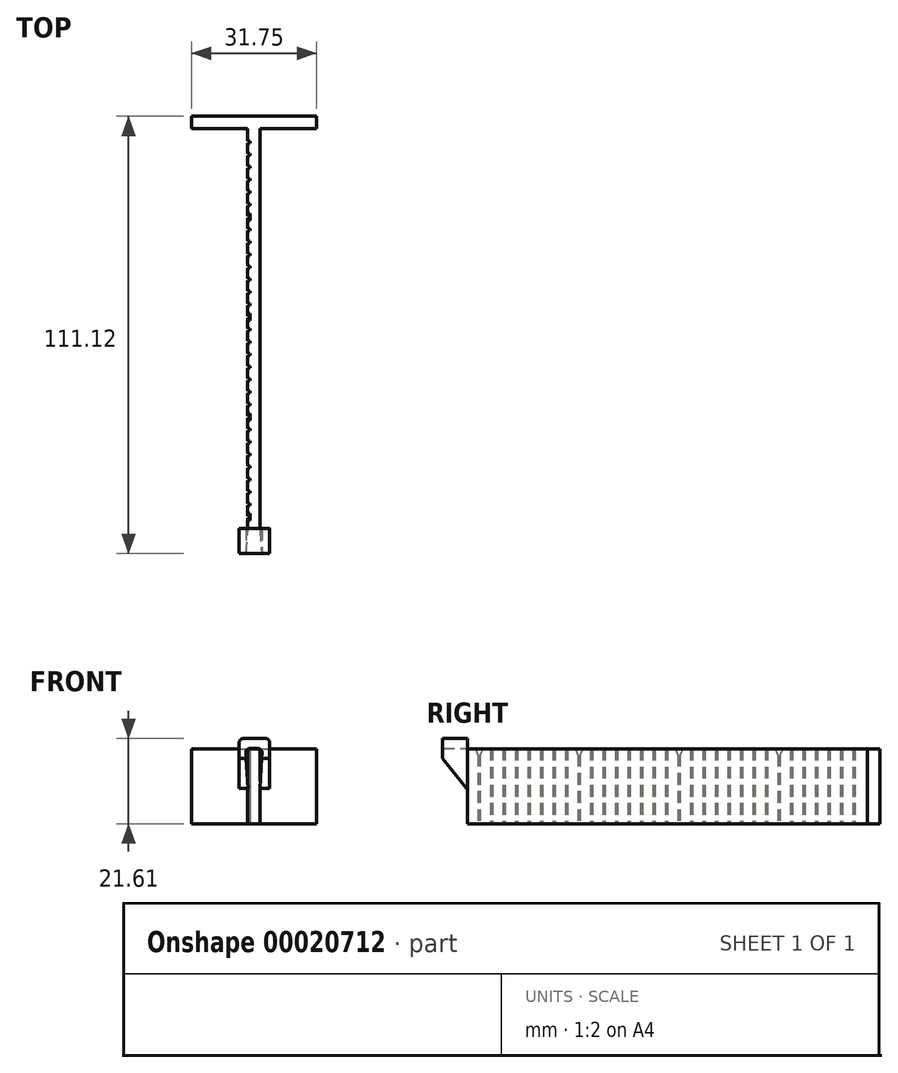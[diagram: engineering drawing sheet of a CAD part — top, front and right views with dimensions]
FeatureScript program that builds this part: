
annotation { "Feature Type Name" : "Feature", "Feature Type Description" : "" }
export const myFeature = defineFeature(function(context is Context, id is Id, definition is map)
    precondition{}
    {
        {
            var Q0;
            Q0=qCreatedBy(makeId("Top.planeOp"),FACE);
            var sketch = newSketch(context, id + "F0", { "sketchPlane" : qUnion([Q0])});
            skLineSegment(sketch, "E0.bottom", {"start": v(0, 0) * mm, "end": v(31.75, 0) * mm});
            skLineSegment(sketch, "E0.top", {"start": v(0, 3.18) * mm, "end": v(31.75, 3.18) * mm});
            skLineSegment(sketch, "E0.left", {"start": v(0, 0) * mm, "end": v(0, 3.18) * mm});
            skLineSegment(sketch, "E0.right", {"start": v(31.75, 0) * mm, "end": v(31.75, 3.18) * mm});
            skLineSegment(sketch, "E1.bottom", {"start": v(14.29, 0) * mm, "end": v(17.46, 0) * mm});
            skLineSegment(sketch, "E1.top", {"start": v(14.29, -101.6) * mm, "end": v(17.46, -101.6) * mm});
            skLineSegment(sketch, "E1.left", {"start": v(14.29, 0) * mm, "end": v(14.29, -101.6) * mm});
            skLineSegment(sketch, "E1.right", {"start": v(17.46, 0) * mm, "end": v(17.46, -101.6) * mm});
            skLineSegment(sketch, "E2", {"start": v(15.87, 3.18) * mm, "end": v(15.88, -34.56) * mm, "construction": true});
            skSolve(sketch);
        }
        {
            var Q0;
            Q0 = qSketchRegion(id + "F0", true);
            extrude(context, id + "F1", {"entities" : qUnion([Q0]), "depth" : 19.05 * mm});
        }
        {
            var Q0;
            Q0=makeQuery(id+"F1.opExtrude","SWEPT_FACE",FACE,{"disambiguationData":[OSD([sQuery(id+"F0.wireOp",EDGE,"E1.left")])]});
            var sketch = newSketch(context, id + "F2", { "sketchPlane" : qUnion([Q0])});
            skLineSegment(sketch, "E3.bottom", {"start": v(3.18, 19.05) * mm, "end": v(3.68, 19.05) * mm});
            skLineSegment(sketch, "E3.top", {"start": v(3.18, 0) * mm, "end": v(3.68, 0) * mm});
            skLineSegment(sketch, "E3.left", {"start": v(3.18, 19.05) * mm, "end": v(3.18, 0) * mm});
            skLineSegment(sketch, "E3.right", {"start": v(3.68, 19.05) * mm, "end": v(3.68, 0) * mm});
            skLineSegment(sketch, "E4.1.0.0", {"start": v(6.35, 19.05) * mm, "end": v(6.35, 0) * mm});
            skLineSegment(sketch, "E4.1.0.1", {"start": v(6.86, 19.05) * mm, "end": v(6.86, 0) * mm});
            skLineSegment(sketch, "E4.1.0.2", {"start": v(6.35, 19.05) * mm, "end": v(6.86, 19.05) * mm});
            skLineSegment(sketch, "E4.1.0.3", {"start": v(6.35, 0) * mm, "end": v(6.86, 0) * mm});
            skLineSegment(sketch, "E4.2.0.0", {"start": v(9.53, 19.05) * mm, "end": v(9.53, 0) * mm});
            skLineSegment(sketch, "E4.2.0.1", {"start": v(10.03, 19.05) * mm, "end": v(10.03, 0) * mm});
            skLineSegment(sketch, "E4.2.0.2", {"start": v(9.53, 19.05) * mm, "end": v(10.03, 19.05) * mm});
            skLineSegment(sketch, "E4.2.0.3", {"start": v(9.53, 0) * mm, "end": v(10.03, 0) * mm});
            skLineSegment(sketch, "E4.3.0.0", {"start": v(12.7, 19.05) * mm, "end": v(12.7, 0) * mm});
            skLineSegment(sketch, "E4.3.0.1", {"start": v(13.2, 19.05) * mm, "end": v(13.2, 0) * mm});
            skLineSegment(sketch, "E4.3.0.2", {"start": v(12.7, 19.05) * mm, "end": v(13.2, 19.05) * mm});
            skLineSegment(sketch, "E4.3.0.3", {"start": v(12.7, 0) * mm, "end": v(13.2, 0) * mm});
            skLineSegment(sketch, "E4.4.0.0", {"start": v(15.88, 19.05) * mm, "end": v(15.88, 0) * mm});
            skLineSegment(sketch, "E4.4.0.1", {"start": v(16.38, 19.05) * mm, "end": v(16.38, 0) * mm});
            skLineSegment(sketch, "E4.4.0.2", {"start": v(15.88, 19.05) * mm, "end": v(16.38, 19.05) * mm});
            skLineSegment(sketch, "E4.4.0.3", {"start": v(15.88, 0) * mm, "end": v(16.38, 0) * mm});
            skLineSegment(sketch, "E4.5.0.0", {"start": v(19.05, 19.05) * mm, "end": v(19.05, 0) * mm});
            skLineSegment(sketch, "E4.5.0.1", {"start": v(19.56, 19.05) * mm, "end": v(19.56, 0) * mm});
            skLineSegment(sketch, "E4.5.0.2", {"start": v(19.05, 19.05) * mm, "end": v(19.56, 19.05) * mm});
            skLineSegment(sketch, "E4.5.0.3", {"start": v(19.05, 0) * mm, "end": v(19.56, 0) * mm});
            skLineSegment(sketch, "E4.6.0.0", {"start": v(22.23, 17.48) * mm, "end": v(22.23, 0) * mm});
            skLineSegment(sketch, "E4.6.0.1", {"start": v(22.73, 17.48) * mm, "end": v(22.73, 0) * mm});
            skLineSegment(sketch, "E4.6.0.3", {"start": v(22.23, 0) * mm, "end": v(22.73, 0) * mm});
            skLineSegment(sketch, "E4.7.0.0", {"start": v(25.4, 19.05) * mm, "end": v(25.4, 0) * mm});
            skLineSegment(sketch, "E4.7.0.1", {"start": v(25.9, 19.05) * mm, "end": v(25.9, 0) * mm});
            skLineSegment(sketch, "E4.7.0.2", {"start": v(25.4, 19.05) * mm, "end": v(25.9, 19.05) * mm});
            skLineSegment(sketch, "E4.7.0.3", {"start": v(25.4, 0) * mm, "end": v(25.9, 0) * mm});
            skLineSegment(sketch, "E4.8.0.0", {"start": v(28.58, 19.05) * mm, "end": v(28.58, 0) * mm});
            skLineSegment(sketch, "E4.8.0.1", {"start": v(29.08, 19.05) * mm, "end": v(29.08, 0) * mm});
            skLineSegment(sketch, "E4.8.0.2", {"start": v(28.58, 19.05) * mm, "end": v(29.08, 19.05) * mm});
            skLineSegment(sketch, "E4.8.0.3", {"start": v(28.58, 0) * mm, "end": v(29.08, 0) * mm});
            skLineSegment(sketch, "E4.9.0.0", {"start": v(31.75, 19.05) * mm, "end": v(31.75, 0) * mm});
            skLineSegment(sketch, "E4.9.0.1", {"start": v(32.26, 19.05) * mm, "end": v(32.26, 0) * mm});
            skLineSegment(sketch, "E4.9.0.2", {"start": v(31.75, 19.05) * mm, "end": v(32.26, 19.05) * mm});
            skLineSegment(sketch, "E4.9.0.3", {"start": v(31.75, 0) * mm, "end": v(32.26, 0) * mm});
            skLineSegment(sketch, "E4.10.0.0", {"start": v(34.93, 19.05) * mm, "end": v(34.93, 0) * mm});
            skLineSegment(sketch, "E4.10.0.1", {"start": v(35.43, 19.05) * mm, "end": v(35.43, 0) * mm});
            skLineSegment(sketch, "E4.10.0.2", {"start": v(34.93, 19.05) * mm, "end": v(35.43, 19.05) * mm});
            skLineSegment(sketch, "E4.10.0.3", {"start": v(34.93, 0) * mm, "end": v(35.43, 0) * mm});
            skLineSegment(sketch, "E4.11.0.0", {"start": v(38.1, 19.05) * mm, "end": v(38.1, 0) * mm});
            skLineSegment(sketch, "E4.11.0.1", {"start": v(38.6, 19.05) * mm, "end": v(38.6, 0) * mm});
            skLineSegment(sketch, "E4.11.0.2", {"start": v(38.1, 19.05) * mm, "end": v(38.6, 19.05) * mm});
            skLineSegment(sketch, "E4.11.0.3", {"start": v(38.1, 0) * mm, "end": v(38.6, 0) * mm});
            skLineSegment(sketch, "E4.12.0.0", {"start": v(41.28, 19.05) * mm, "end": v(41.28, 0) * mm});
            skLineSegment(sketch, "E4.12.0.1", {"start": v(41.78, 19.05) * mm, "end": v(41.78, 0) * mm});
            skLineSegment(sketch, "E4.12.0.2", {"start": v(41.28, 19.05) * mm, "end": v(41.78, 19.05) * mm});
            skLineSegment(sketch, "E4.12.0.3", {"start": v(41.28, 0) * mm, "end": v(41.78, 0) * mm});
            skLineSegment(sketch, "E4.13.0.0", {"start": v(44.45, 19.05) * mm, "end": v(44.45, 0) * mm});
            skLineSegment(sketch, "E4.13.0.1", {"start": v(44.96, 19.05) * mm, "end": v(44.96, 0) * mm});
            skLineSegment(sketch, "E4.13.0.2", {"start": v(44.45, 19.05) * mm, "end": v(44.96, 19.05) * mm});
            skLineSegment(sketch, "E4.13.0.3", {"start": v(44.45, 0) * mm, "end": v(44.96, 0) * mm});
            skLineSegment(sketch, "E4.14.0.0", {"start": v(47.63, 19.05) * mm, "end": v(47.63, 0) * mm});
            skLineSegment(sketch, "E4.14.0.1", {"start": v(48.13, 19.05) * mm, "end": v(48.13, 0) * mm});
            skLineSegment(sketch, "E4.14.0.2", {"start": v(47.63, 19.05) * mm, "end": v(48.13, 19.05) * mm});
            skLineSegment(sketch, "E4.14.0.3", {"start": v(47.63, 0) * mm, "end": v(48.13, 0) * mm});
            skLineSegment(sketch, "E4.15.0.0", {"start": v(50.8, 19.05) * mm, "end": v(50.8, 0) * mm});
            skLineSegment(sketch, "E4.15.0.1", {"start": v(51.3, 19.05) * mm, "end": v(51.3, 0) * mm});
            skLineSegment(sketch, "E4.15.0.2", {"start": v(50.8, 19.05) * mm, "end": v(51.3, 19.05) * mm});
            skLineSegment(sketch, "E4.15.0.3", {"start": v(50.8, 0) * mm, "end": v(51.3, 0) * mm});
            skLineSegment(sketch, "E4.16.0.0", {"start": v(53.98, 19.05) * mm, "end": v(53.98, 0) * mm});
            skLineSegment(sketch, "E4.16.0.1", {"start": v(54.48, 19.05) * mm, "end": v(54.48, 0) * mm});
            skLineSegment(sketch, "E4.16.0.2", {"start": v(53.98, 19.05) * mm, "end": v(54.48, 19.05) * mm});
            skLineSegment(sketch, "E4.16.0.3", {"start": v(53.98, 0) * mm, "end": v(54.48, 0) * mm});
            skLineSegment(sketch, "E4.17.0.0", {"start": v(57.15, 19.05) * mm, "end": v(57.15, 0) * mm});
            skLineSegment(sketch, "E4.17.0.1", {"start": v(57.66, 19.05) * mm, "end": v(57.66, 0) * mm});
            skLineSegment(sketch, "E4.17.0.2", {"start": v(57.15, 19.05) * mm, "end": v(57.66, 19.05) * mm});
            skLineSegment(sketch, "E4.17.0.3", {"start": v(57.15, 0) * mm, "end": v(57.66, 0) * mm});
            skLineSegment(sketch, "E4.18.0.0", {"start": v(60.33, 19.05) * mm, "end": v(60.33, 0) * mm});
            skLineSegment(sketch, "E4.18.0.1", {"start": v(60.83, 19.05) * mm, "end": v(60.83, 0) * mm});
            skLineSegment(sketch, "E4.18.0.2", {"start": v(60.33, 19.05) * mm, "end": v(60.83, 19.05) * mm});
            skLineSegment(sketch, "E4.18.0.3", {"start": v(60.33, 0) * mm, "end": v(60.83, 0) * mm});
            skLineSegment(sketch, "E4.19.0.0", {"start": v(63.5, 19.05) * mm, "end": v(63.5, 0) * mm});
            skLineSegment(sketch, "E4.19.0.1", {"start": v(64, 19.05) * mm, "end": v(64, 0) * mm});
            skLineSegment(sketch, "E4.19.0.2", {"start": v(63.5, 19.05) * mm, "end": v(64, 19.05) * mm});
            skLineSegment(sketch, "E4.19.0.3", {"start": v(63.5, 0) * mm, "end": v(64, 0) * mm});
            skLineSegment(sketch, "E4.20.0.0", {"start": v(66.68, 19.05) * mm, "end": v(66.68, 0) * mm});
            skLineSegment(sketch, "E4.20.0.1", {"start": v(67.18, 19.05) * mm, "end": v(67.18, 0) * mm});
            skLineSegment(sketch, "E4.20.0.2", {"start": v(66.68, 19.05) * mm, "end": v(67.18, 19.05) * mm});
            skLineSegment(sketch, "E4.20.0.3", {"start": v(66.68, 0) * mm, "end": v(67.18, 0) * mm});
            skLineSegment(sketch, "E4.21.0.0", {"start": v(69.85, 19.05) * mm, "end": v(69.85, 0) * mm});
            skLineSegment(sketch, "E4.21.0.1", {"start": v(70.36, 19.05) * mm, "end": v(70.36, 0) * mm});
            skLineSegment(sketch, "E4.21.0.2", {"start": v(69.85, 19.05) * mm, "end": v(70.36, 19.05) * mm});
            skLineSegment(sketch, "E4.21.0.3", {"start": v(69.85, 0) * mm, "end": v(70.36, 0) * mm});
            skLineSegment(sketch, "E4.22.0.0", {"start": v(73.03, 19.05) * mm, "end": v(73.03, 0) * mm});
            skLineSegment(sketch, "E4.22.0.1", {"start": v(73.53, 19.05) * mm, "end": v(73.53, 0) * mm});
            skLineSegment(sketch, "E4.22.0.2", {"start": v(73.03, 19.05) * mm, "end": v(73.53, 19.05) * mm});
            skLineSegment(sketch, "E4.22.0.3", {"start": v(73.03, 0) * mm, "end": v(73.53, 0) * mm});
            skLineSegment(sketch, "E4.23.0.0", {"start": v(76.2, 19.05) * mm, "end": v(76.2, 0) * mm});
            skLineSegment(sketch, "E4.23.0.1", {"start": v(76.7, 19.05) * mm, "end": v(76.7, 0) * mm});
            skLineSegment(sketch, "E4.23.0.2", {"start": v(76.2, 19.05) * mm, "end": v(76.7, 19.05) * mm});
            skLineSegment(sketch, "E4.23.0.3", {"start": v(76.2, 0) * mm, "end": v(76.7, 0) * mm});
            skLineSegment(sketch, "E4.24.0.0", {"start": v(79.38, 19.05) * mm, "end": v(79.38, 0) * mm});
            skLineSegment(sketch, "E4.24.0.1", {"start": v(79.88, 19.05) * mm, "end": v(79.88, 0) * mm});
            skLineSegment(sketch, "E4.24.0.2", {"start": v(79.38, 19.05) * mm, "end": v(79.88, 19.05) * mm});
            skLineSegment(sketch, "E4.24.0.3", {"start": v(79.38, 0) * mm, "end": v(79.88, 0) * mm});
            skLineSegment(sketch, "E4.25.0.0", {"start": v(82.55, 19.05) * mm, "end": v(82.55, 0) * mm});
            skLineSegment(sketch, "E4.25.0.1", {"start": v(83.06, 19.05) * mm, "end": v(83.06, 0) * mm});
            skLineSegment(sketch, "E4.25.0.2", {"start": v(82.55, 19.05) * mm, "end": v(83.06, 19.05) * mm});
            skLineSegment(sketch, "E4.25.0.3", {"start": v(82.55, 0) * mm, "end": v(83.06, 0) * mm});
            skLineSegment(sketch, "E4.26.0.0", {"start": v(85.73, 19.05) * mm, "end": v(85.73, 0) * mm});
            skLineSegment(sketch, "E4.26.0.1", {"start": v(86.23, 19.05) * mm, "end": v(86.23, 0) * mm});
            skLineSegment(sketch, "E4.26.0.2", {"start": v(85.73, 19.05) * mm, "end": v(86.23, 19.05) * mm});
            skLineSegment(sketch, "E4.26.0.3", {"start": v(85.73, 0) * mm, "end": v(86.23, 0) * mm});
            skLineSegment(sketch, "E4.27.0.0", {"start": v(88.9, 19.05) * mm, "end": v(88.9, 0) * mm});
            skLineSegment(sketch, "E4.27.0.1", {"start": v(89.4, 19.05) * mm, "end": v(89.4, 0) * mm});
            skLineSegment(sketch, "E4.27.0.2", {"start": v(88.9, 19.05) * mm, "end": v(89.4, 19.05) * mm});
            skLineSegment(sketch, "E4.27.0.3", {"start": v(88.9, 0) * mm, "end": v(89.4, 0) * mm});
            skLineSegment(sketch, "E4.28.0.0", {"start": v(92.08, 19.05) * mm, "end": v(92.08, 0) * mm});
            skLineSegment(sketch, "E4.28.0.1", {"start": v(92.58, 19.05) * mm, "end": v(92.58, 0) * mm});
            skLineSegment(sketch, "E4.28.0.2", {"start": v(92.08, 19.05) * mm, "end": v(92.58, 19.05) * mm});
            skLineSegment(sketch, "E4.28.0.3", {"start": v(92.08, 0) * mm, "end": v(92.58, 0) * mm});
            skLineSegment(sketch, "E4.29.0.0", {"start": v(95.25, 19.05) * mm, "end": v(95.25, 0) * mm});
            skLineSegment(sketch, "E4.29.0.1", {"start": v(95.76, 19.05) * mm, "end": v(95.76, 0) * mm});
            skLineSegment(sketch, "E4.29.0.2", {"start": v(95.25, 19.05) * mm, "end": v(95.76, 19.05) * mm});
            skLineSegment(sketch, "E4.29.0.3", {"start": v(95.25, 0) * mm, "end": v(95.76, 0) * mm});
            skLineSegment(sketch, "E4.direction1", {"start": v(3.18, 0) * mm, "end": v(6.35, 0) * mm, "construction": true});
            skLineSegment(sketch, "E5", {"start": v(21.5, 19.05) * mm, "end": v(22.23, 17.48) * mm});
            skLineSegment(sketch, "E6", {"start": v(22.73, 17.48) * mm, "end": v(23.3, 19.05) * mm});
            skLineSegment(sketch, "E7", {"start": v(22.23, 17.48) * mm, "end": v(22.73, 17.48) * mm});
            skLineSegment(sketch, "E8", {"start": v(23.3, 19.05) * mm, "end": v(21.5, 19.05) * mm});
            skLineSegment(sketch, "E9.1.0.0", {"start": v(48.7, 19.05) * mm, "end": v(46.9, 19.05) * mm});
            skLineSegment(sketch, "E9.1.0.1", {"start": v(46.9, 19.05) * mm, "end": v(47.63, 17.48) * mm});
            skLineSegment(sketch, "E9.1.0.2", {"start": v(48.13, 17.48) * mm, "end": v(48.7, 19.05) * mm});
            skLineSegment(sketch, "E9.1.0.3", {"start": v(47.63, 17.48) * mm, "end": v(48.13, 17.48) * mm});
            skLineSegment(sketch, "E9.2.0.0", {"start": v(74.1, 19.05) * mm, "end": v(72.3, 19.05) * mm});
            skLineSegment(sketch, "E9.2.0.1", {"start": v(72.3, 19.05) * mm, "end": v(73.03, 17.48) * mm});
            skLineSegment(sketch, "E9.2.0.2", {"start": v(73.53, 17.48) * mm, "end": v(74.1, 19.05) * mm});
            skLineSegment(sketch, "E9.2.0.3", {"start": v(73.03, 17.48) * mm, "end": v(73.53, 17.48) * mm});
            skLineSegment(sketch, "E9.3.0.0", {"start": v(99.5, 19.05) * mm, "end": v(97.7, 19.05) * mm});
            skLineSegment(sketch, "E9.3.0.1", {"start": v(97.7, 19.05) * mm, "end": v(98.43, 17.48) * mm});
            skLineSegment(sketch, "E9.3.0.2", {"start": v(98.93, 17.48) * mm, "end": v(99.5, 19.05) * mm});
            skLineSegment(sketch, "E9.3.0.3", {"start": v(98.43, 17.48) * mm, "end": v(98.93, 17.48) * mm});
            skLineSegment(sketch, "E9.direction1", {"start": v(22.23, 17.48) * mm, "end": v(47.63, 17.48) * mm, "construction": true});
            skLineSegment(sketch, "E10.0.30.0", {"start": v(98.43, 19.05) * mm, "end": v(98.43, 0) * mm});
            skLineSegment(sketch, "E10.3.30.0", {"start": v(98.93, 19.05) * mm, "end": v(98.93, 0) * mm});
            skLineSegment(sketch, "E10.6.30.0", {"start": v(98.43, 19.05) * mm, "end": v(98.93, 19.05) * mm});
            skLineSegment(sketch, "E10.9.30.0", {"start": v(98.43, 0) * mm, "end": v(98.93, 0) * mm});
            skSolve(sketch);
        }
        {
            var Q0;
            Q0 = qSketchRegion(id + "F2", true);
            extrude(context, id + "F3", {"entities" : qUnion([Q0]), "operationType" : NewBodyOperationType.REMOVE, "oppositeDirection" : true, "depth" : 0.5 * mm});
        }
        {
            var Q0;
            Q0=makeQuery(id+"F1.opExtrude","SWEPT_FACE",FACE,{"disambiguationData":[OSD([sQuery(id+"F0.wireOp",EDGE,"E1.top")])]});
            var sketch = newSketch(context, id + "F4", { "sketchPlane" : qUnion([Q0])});
            skLineSegment(sketch, "E11.right", {"start": v(12.1, 8.91) * mm, "end": v(12.1, 21.61) * mm});
            skLineSegment(sketch, "E12.right", {"start": v(19.85, 8.91) * mm, "end": v(19.85, 21.61) * mm});
            skLineSegment(sketch, "E13", {"start": v(17.95, 19.07) * mm, "end": v(17.36, 8.9) * mm});
            skLineSegment(sketch, "E14", {"start": v(12.1, 21.61) * mm, "end": v(19.85, 21.61) * mm});
            skLineSegment(sketch, "E15", {"start": v(13.71, 19.07) * mm, "end": v(17.95, 19.07) * mm});
            skPoint(sketch, "E16.end.orphan", {"position": v(14.29, 8.9) * mm});
            skPoint(sketch, "E12.bottom.start.orphan", {"position": v(17.46, 8.9) * mm});
            skLineSegment(sketch, "E17.trimOffspring", {"start": v(17.36, 8.9) * mm, "end": v(19.85, 8.91) * mm});
            skLineSegment(sketch, "E18", {"start": v(12.1, 8.91) * mm, "end": v(14.37, 8.91) * mm});
            skLineSegment(sketch, "E19", {"start": v(14.37, 8.91) * mm, "end": v(13.71, 19.07) * mm});
            skSolve(sketch);
        }
        {
            var Q0;
            Q0 = qSketchRegion(id + "F4", true);
            extrude(context, id + "F5", {"entities" : qUnion([Q0]), "depth" : 6.35 * mm});
        }
        {
            var Q0;
            Q0=makeQuery(id+"F5.opExtrude","CAP_EDGE",EDGE,{"disambiguationData":[OSD([sQuery(id+"F4.wireOp",EDGE,"E18")])],"isStart":false});
            var Q1;
            Q1=makeQuery(id+"F5.opExtrude","CAP_EDGE",EDGE,{"disambiguationData":[OSD([sQuery(id+"F4.wireOp",EDGE,"E17.trimOffspring")])],"isStart":false});
            chamfer(context, id + "F6", {"entities" : qUnion([Q0, Q1]), "chamferType" : ChamferType.TWO_OFFSETS, "width1" : 7.62 * mm, "oppositeDirection" : false, "width2" : 6.1 * mm, "tangentPropagation" : true});
        }
        {
            var Q0;
            Q0=makeQuery(id+"F5.opExtrude","SWEPT_EDGE",EDGE,{"disambiguationData":[OSD([sQuery(id+"F4.wireOp",EDGE,"E13"),sQuery(id+"F4.wireOp",EDGE,"E15")])]});
            var Q1;
            Q1=makeQuery(id+"F5.opExtrude","SWEPT_EDGE",EDGE,{"disambiguationData":[OSD([sQuery(id+"F4.wireOp",EDGE,"E15"),sQuery(id+"F4.wireOp",EDGE,"E19")])]});
            var Q2;
            Q2=makeQuery(id+"F5.opExtrude","SWEPT_EDGE",EDGE,{"disambiguationData":[OSD([sQuery(id+"F4.wireOp",EDGE,"E12.right"),sQuery(id+"F4.wireOp",EDGE,"E14")])]});
            var Q3;
            Q3=makeQuery(id+"F5.opExtrude","SWEPT_EDGE",EDGE,{"disambiguationData":[OSD([sQuery(id+"F4.wireOp",EDGE,"E11.right"),sQuery(id+"F4.wireOp",EDGE,"E14")])]});
            fillet(context, id + "F7", {"entities" : qUnion([Q0, Q1, Q2, Q3]), "radius" : 1.02 * mm, "tangentPropagation" : true, "allowEdgeOverflow" : false});
        }
    });
